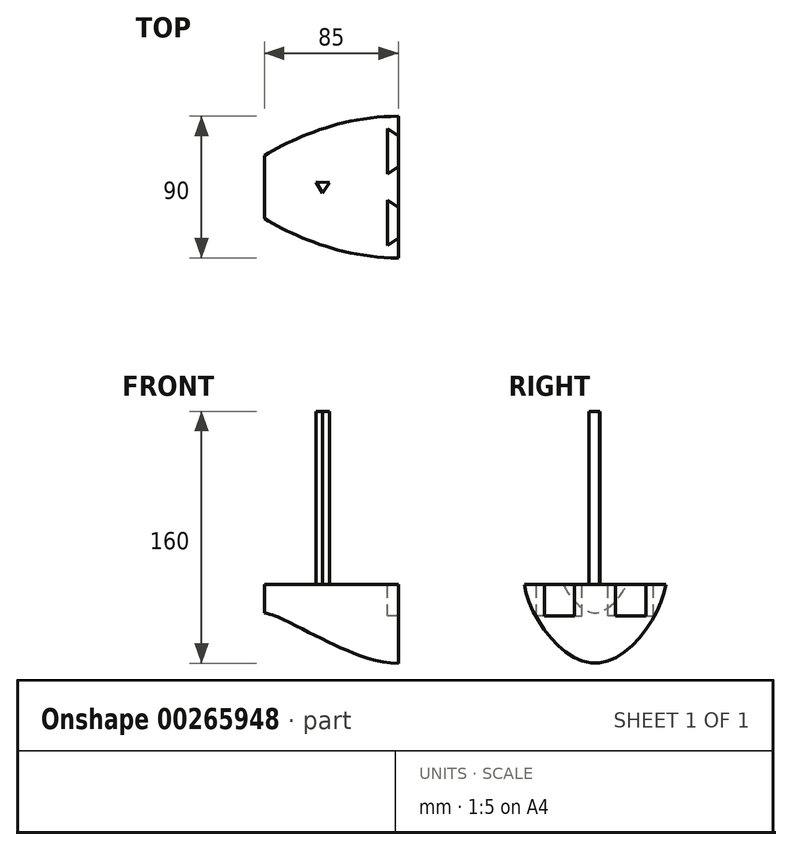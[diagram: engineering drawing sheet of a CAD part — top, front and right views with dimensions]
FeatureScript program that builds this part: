
annotation { "Feature Type Name" : "Feature", "Feature Type Description" : "" }
export const myFeature = defineFeature(function(context is Context, id is Id, definition is map)
    precondition{}
    {
        {
            var Q0;
            Q0=qCreatedBy(makeId("Right.planeOp"),FACE);
            cPlane(context, id + "F0", {"entities" : qUnion([Q0]), "cplaneType" : CPlaneType.OFFSET, "offset" : 85 * mm, "oppositeDirection" : true, "width" : 150 * mm, "height" : 150 * mm});
        }
        {
            var Q0;
            Q0=qCreatedBy(makeId("Right.planeOp"),FACE);
            var sketch = newSketch(context, id + "F1", { "sketchPlane" : qUnion([Q0])});
            skFitSpline(sketch, "E0", {"points": [v(-45, 0) * mm, v(0, -50) * mm, v(45, 0) * mm], "startDerivative": vector(18, -120) * mm, "endDerivative": vector(18, 120) * mm});
            skFitSpline(sketch, "E1", {"points": [v(-45, 0) * mm, v(0, 0) * mm, v(45, 0) * mm], "startDerivative": vector(90, 0) * mm, "endDerivative": vector(90, 0) * mm});
            skSolve(sketch);
        }
        {
            var Q0;
            Q0=qCreatedBy(id+"F0.planeOp",FACE);
            var sketch = newSketch(context, id + "F2", { "sketchPlane" : qUnion([Q0])});
            skFitSpline(sketch, "E2", {"points": [v(-20, 0) * mm, v(0, -18) * mm, v(20, 0) * mm], "startDerivative": vector(12, -30) * mm, "endDerivative": vector(12, 30) * mm});
            skFitSpline(sketch, "E3", {"points": [v(-20, 0) * mm, v(0, 0) * mm, v(20, 0) * mm], "startDerivative": vector(40, 0) * mm, "endDerivative": vector(40, 0) * mm});
            skSolve(sketch);
        }
        {
            var Q0;
            Q0=qCreatedBy(makeId("Front.planeOp"),FACE);
            var sketch = newSketch(context, id + "F3", { "sketchPlane" : qUnion([Q0])});
            skFitSpline(sketch, "E4", {"points": [v(-85, -18) * mm, v(0, -50) * mm], "startDerivative": vector(45, -6) * mm, "endDerivative": vector(88.93, 0) * mm});
            skSolve(sketch);
        }
        {
            var Q0;
            Q0=qCreatedBy(makeId("Top.planeOp"),FACE);
            var sketch = newSketch(context, id + "F4", { "sketchPlane" : qUnion([Q0])});
            skFitSpline(sketch, "E5", {"points": [v(-85, 20) * mm, v(0, 45) * mm], "startDerivative": vector(60, 36) * mm, "endDerivative": vector(105, 0) * mm});
            skFitSpline(sketch, "E6.MirrorCS", {"points": [v(-85, -20) * mm, v(0, -45) * mm], "startDerivative": vector(60, -36) * mm, "endDerivative": vector(105, 0) * mm});
            skSolve(sketch);
        }
        {
            var Q0;
            Q0=makeQuery(id+"F1.imprint","IMPRINT",FACE,{"disambiguationData":[TD([[makeQuery(id+"F1.imprint","IMPRINT",EDGE,{"derivedFrom":sQuery(id+"F1.wireOp",EDGE,"E0")}),1.0]])]});
            var Q1;
            Q1=makeQuery(id+"F2.imprint","IMPRINT",FACE,{"disambiguationData":[TD([[makeQuery(id+"F2.imprint","IMPRINT",EDGE,{"derivedFrom":sQuery(id+"F2.wireOp",EDGE,"E2")}),1.0]])]});
            var Q2;
            Q2=sQuery(id+"F3.wireOp",EDGE,"E4");
            var Q3;
            Q3=sQuery(id+"F4.wireOp",EDGE,"E6.MirrorCS");
            var Q4;
            Q4=sQuery(id+"F4.wireOp",EDGE,"E5");
            loft(context, id + "F5", {"addGuides" : true, "sheetProfilesArray" : [{ "sheetProfileEntities" : qUnion([Q0]) }, { "sheetProfileEntities" : qUnion([Q1]) }], "guidesArray" : [{ "guideEntities" : qUnion([Q2]), "guideDerivativeType" : LoftGuideDerivativeType.DEFAULT, "guideDerivativeMagnitude" : 1 }, { "guideEntities" : qUnion([Q3]), "guideDerivativeType" : LoftGuideDerivativeType.DEFAULT, "guideDerivativeMagnitude" : 1 }, { "guideEntities" : qUnion([Q4]), "guideDerivativeType" : LoftGuideDerivativeType.DEFAULT, "guideDerivativeMagnitude" : 1 }]});
        }
        {
            var Q0;
            Q0=makeQuery(id+"F5.opLoft","SWEPT_FACE",FACE,{"disambiguationData":[OSD([sQuery(id+"F1.wireOp",EDGE,"E1"),sQuery(id+"F2.wireOp",EDGE,"E3"),sQuery(id+"F4.wireOp",EDGE,"E5"),sQuery(id+"F4.wireOp",EDGE,"E6.MirrorCS")])]});
            var sketch = newSketch(context, id + "F6", { "sketchPlane" : qUnion([Q0])});
            skLineSegment(sketch, "E7", {"start": v(0, 32.3) * mm, "end": v(-6.7, 37.1) * mm});
            skLineSegment(sketch, "E8", {"start": v(-6.7, 37.1) * mm, "end": v(-6.7, 22.66) * mm});
            skLineSegment(sketch, "E9.MirrorCS", {"start": v(-6.7, 8.21) * mm, "end": v(-6.7, 22.66) * mm});
            skLineSegment(sketch, "E10.MirrorCS", {"start": v(0, 13.03) * mm, "end": v(-6.7, 8.21) * mm});
            skSolve(sketch);
        }
        {
            var Q0;
            {var subQ1=sQuery(id+"F6.wireOp",EDGE,"E7");Q0=makeQuery(id+"F6.imprint","IMPRINT",FACE,{"disambiguationData":[TD([[makeQuery(id+"F6.imprint","IMPRINT",EDGE,{"derivedFrom":subQ1}),1.0]])]});}
            extrude(context, id + "F7", {"entities" : qUnion([Q0]), "operationType" : NewBodyOperationType.REMOVE, "oppositeDirection" : true, "depth" : 20 * mm});
        }
        {
            var Q0;
            Q0=makeQuery(id+"F5.opLoft","SWEPT_FACE",FACE,{"disambiguationData":[OSD([sQuery(id+"F1.wireOp",EDGE,"E1"),sQuery(id+"F2.wireOp",EDGE,"E3"),sQuery(id+"F4.wireOp",EDGE,"E5"),sQuery(id+"F4.wireOp",EDGE,"E6.MirrorCS")])]});
            var sketch = newSketch(context, id + "F8", { "sketchPlane" : qUnion([Q0])});
            skLineSegment(sketch, "E11", {"start": v(0, -13.03) * mm, "end": v(-6.7, -8.21) * mm});
            skLineSegment(sketch, "E12", {"start": v(-6.7, -8.21) * mm, "end": v(-6.7, -37.1) * mm});
            skLineSegment(sketch, "E13", {"start": v(-6.7, -37.1) * mm, "end": v(0, -32.3) * mm});
            skSolve(sketch);
        }
        {
            var Q0;
            {var subQ0=sQuery(id+"F8.wireOp",EDGE,"E11");Q0=makeQuery(id+"F8.imprint","IMPRINT",FACE,{"disambiguationData":[TD([[makeQuery(id+"F8.imprint","IMPRINT",EDGE,{"derivedFrom":subQ0}),1.0]])]});}
            extrude(context, id + "F9", {"entities" : qUnion([Q0]), "operationType" : NewBodyOperationType.REMOVE, "oppositeDirection" : true, "depth" : 20 * mm});
        }
        {
            var Q0;
            Q0=makeQuery(id+"F5.opLoft","SWEPT_FACE",FACE,{"disambiguationData":[OSD([sQuery(id+"F1.wireOp",EDGE,"E1"),sQuery(id+"F2.wireOp",EDGE,"E3"),sQuery(id+"F4.wireOp",EDGE,"E5"),sQuery(id+"F4.wireOp",EDGE,"E6.MirrorCS")])]});
            var sketch = newSketch(context, id + "F10", { "sketchPlane" : qUnion([Q0])});
            skLineSegment(sketch, "E14", {"start": v(-52.36, 3.1) * mm, "end": v(-48.06, -3.87) * mm});
            skLineSegment(sketch, "E15", {"start": v(-43.76, 2.89) * mm, "end": v(-48.06, -3.87) * mm});
            skLineSegment(sketch, "E16", {"start": v(-43.76, 2.89) * mm, "end": v(-52.36, 3.1) * mm});
            skSolve(sketch);
        }
        {
            var Q0;
            Q0=makeQuery(id+"F10.imprint","IMPRINT",FACE,{"disambiguationData":[TD([[makeQuery(id+"F10.imprint","IMPRINT",EDGE,{"derivedFrom":sQuery(id+"F10.wireOp",EDGE,"E14")}),1.0]])]});
            extrude(context, id + "F11", {"entities" : qUnion([Q0]), "operationType" : NewBodyOperationType.ADD, "depth" : 110 * mm});
        }
    });
